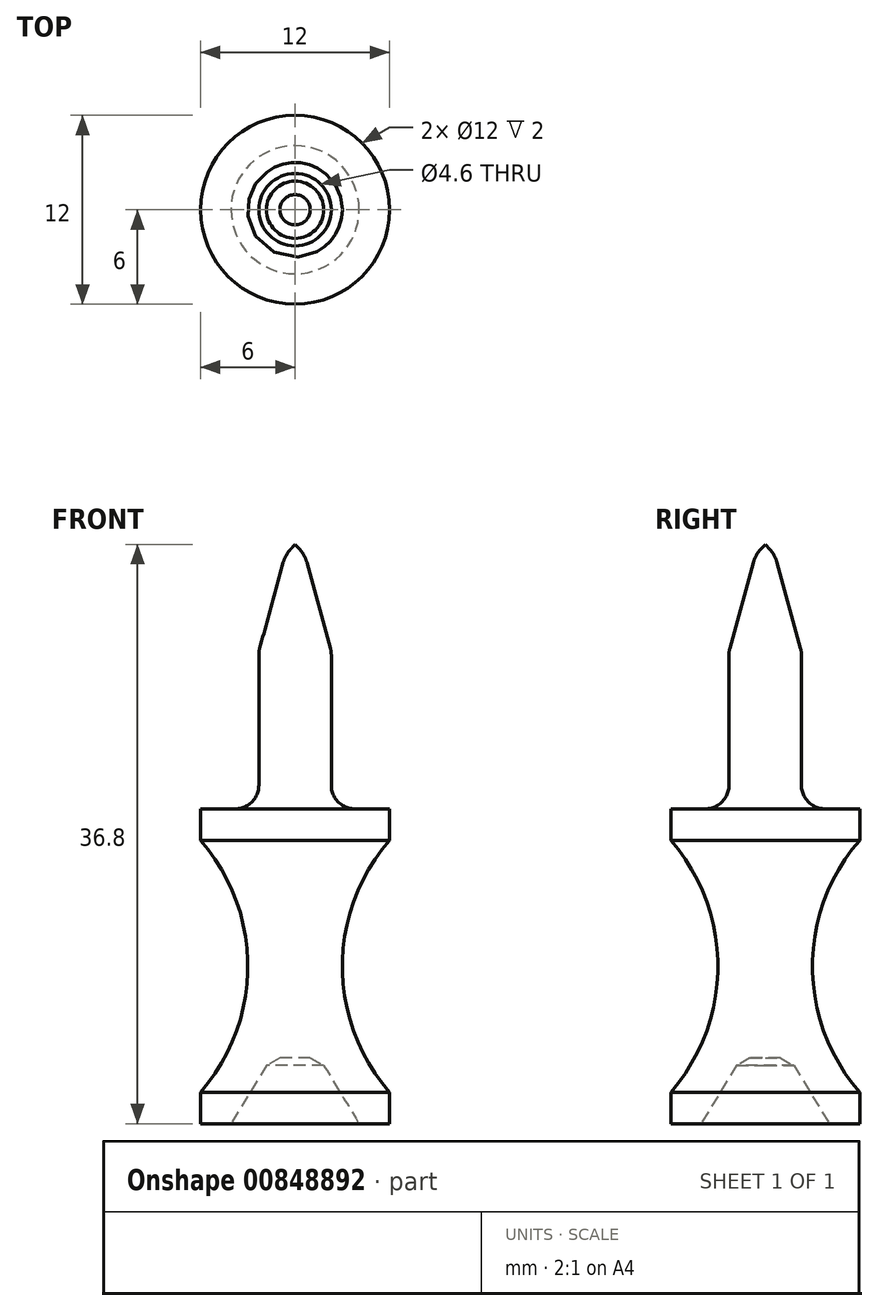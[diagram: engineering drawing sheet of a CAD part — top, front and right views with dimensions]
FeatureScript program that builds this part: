
annotation { "Feature Type Name" : "Feature", "Feature Type Description" : "" }
export const myFeature = defineFeature(function(context is Context, id is Id, definition is map)
    precondition{}
    {
        {
            var Q0;
            Q0=qCreatedBy(makeId("Front.planeOp"),FACE);
            var sketch = newSketch(context, id + "F0", { "sketchPlane" : qUnion([Q0])});
            skLineSegment(sketch, "E0", {"start": v(4.07, 0) * mm, "end": v(6, 0) * mm});
            skLineSegment(sketch, "E1", {"start": v(6, 0) * mm, "end": v(6, 2) * mm});
            skLineSegment(sketch, "E2", {"start": v(6, 2) * mm, "end": v(6, 18) * mm});
            skPoint(sketch, "E3.end.orphan", {"position": v(0, 22.1) * mm});
            skPoint(sketch, "E4.end.orphan", {"position": v(0, 24.82) * mm});
            skLineSegment(sketch, "E5", {"start": v(6, 18) * mm, "end": v(6, 20) * mm});
            skLineSegment(sketch, "E6", {"start": v(6, 20) * mm, "end": v(2.3, 20) * mm});
            skLineSegment(sketch, "E7", {"start": v(2.3, 20) * mm, "end": v(2.3, 30) * mm});
            skPoint(sketch, "E8.end.orphan", {"position": v(0, 31.06) * mm});
            skLineSegment(sketch, "E9", {"start": v(2.3, 30) * mm, "end": v(0.62, 36.1) * mm});
            skLineSegment(sketch, "E10", {"start": v(0, 0) * mm, "end": v(0, 10) * mm});
            skLineSegment(sketch, "E11", {"start": v(0, 10) * mm, "end": v(3, 10) * mm});
            skArc(sketch, "E12", {"start": v(6, 18) * mm, "mid": v(3, 10) * mm, "end": v(6, 2) * mm});
            skLineSegment(sketch, "E13", {"start": v(4.07, 0) * mm, "end": v(1.53, 4.18) * mm});
            skLineSegment(sketch, "E14", {"start": v(1.53, 4.18) * mm, "end": v(0, 4.18) * mm});
            skPoint(sketch, "E14.endSnap0", {"position": v(0, 5) * mm});
            skLineSegment(sketch, "E15", {"start": v(0.62, 36.1) * mm, "end": v(0, 36.8) * mm});
            skPoint(sketch, "E16.orphan", {"position": v(0, 38.37) * mm});
            skSolve(sketch);
        }
        {
            var Q0;
            Q0=sQuery(id+"F0.wireOp",EDGE,"E9");
            var Q1;
            Q1=sQuery(id+"F0.wireOp",EDGE,"E7");
            var Q2;
            Q2=sQuery(id+"F0.wireOp",EDGE,"E5");
            var Q3;
            Q3=sQuery(id+"F0.wireOp",EDGE,"E13");
            var Q4;
            Q4=sQuery(id+"F0.wireOp",EDGE,"E12");
            var Q5;
            Q5=sQuery(id+"F0.wireOp",EDGE,"E1");
            var Q6;
            Q6=sQuery(id+"F0.wireOp",EDGE,"E6");
            var Q7;
            Q7=sQuery(id+"F0.wireOp",EDGE,"E14");
            var Q8;
            Q8=sQuery(id+"F0.wireOp",EDGE,"E0");
            var Q9;
            Q9=sQuery(id+"F0.wireOp",EDGE,"E15");
            var Q10;
            Q10=sQuery(id+"F0.wireOp",EDGE,"E10");
            revolve(context, id + "F1", {"bodyType" : ToolBodyType.SURFACE, "surfaceOperationType" : NewSurfaceOperationType.NEW, "surfaceEntities" : qUnion([Q0, Q1, Q2, Q3, Q4, Q5, Q6, Q7, Q8, Q9]), "axis" : qUnion([Q10]), "revolveType" : RevolveType.FULL});
        }
        {
            var Q0;
            Q0=makeQuery(id+"F1.opRevolve","SWEPT_EDGE",EDGE,{"disambiguationData":[OSD([sQuery(id+"F0.wireOp",VERTEX,"E6.end")])]});
            var Q1;
            Q1=makeQuery(id+"F1.opRevolve","SWEPT_EDGE",EDGE,{"disambiguationData":[OSD([sQuery(id+"F0.wireOp",VERTEX,"E7.end")])]});
            fillet(context, id + "F2", {"entities" : qUnion([Q0, Q1]), "radius" : 1.5 * mm, "tangentPropagation" : true, "allowEdgeOverflow" : false});
        }
        {
            var Q0;
            Q0=makeQuery(id+"F1.opRevolve","SWEPT_EDGE",EDGE,{"disambiguationData":[OSD([sQuery(id+"F0.wireOp",VERTEX,"E14.start")])]});
            chamfer(context, id + "F3", {"entities" : qUnion([Q0]), "width" : 1 * mm, "tangentPropagation" : true});
        }
        {
            var Q0;
            Q0=makeQuery(id+"F1.opRevolve","SWEPT_EDGE",EDGE,{"disambiguationData":[OSD([sQuery(id+"F0.wireOp",VERTEX,"E15.start")])]});
            fillet(context, id + "F4", {"entities" : qUnion([Q0]), "radius" : 2 * mm, "tangentPropagation" : true, "allowEdgeOverflow" : false});
        }
    });
